FCSTD DOCUMENT  (FreeCAD 1.0R39319 (Git))
Label: master
License: All rights reserved
LicenseURL: https://en.wikipedia.org/wiki/All_rights_reserved
objects: Spreadsheet::Sheet×1, App::VarSet×1

FEATURE [Spreadsheet::Sheet] Spreadsheet  label="dims"
  cells = A1='inner chamber width; B1(iwChamber)=70; D1='brick thickness; E1=76; A2='outer chamber width; B2(owChamber)==B1 + 2 * E1; D2='brick width; E2=114; A3='chamber height; B3(hChamber)=150; D3='brick height; E3(hBrick)=210; A4='chamber base thickness; B4(tcBase)==E1; A5='chamber outer height; B5(hcWall)==B3 + B4; D5='extrusion width; E5(wExt)=20; D6='upper height; E6=40; A7='upper panel thickness; B7(tUpperPanel)=2; D7='lower height; E7=20; A8='lower panel thickness; B8(tLowerPanel)=2; A9='base thickness; B9(tBase)=3; D9='chamber proud; E9(brickProud)=5; D10='chamber top thickness; E10(tTop)=3; D11='upper panel trim; E11(uPanelTrim)==E9 + E10 + B7; A12='rockwool thickness; B12(tRockwool)=100; D12='upper panel height; E12(hUpPanel)==B9 + 20 + B5 - E11; A14='frame base width; B14(iwFurnace)==B2 + 2 * B12; A15='chamber edge length; B15(opChamber)==B2 / (1 + sqrt(2)); A16='furnace edge length; B16(opFurnace)==B14 / (1 + sqrt(2)); A18='lower chamber height; B18(lcHeight)=200; A19='lower brace height; B19(lvBrace)==B18 + E6 + E7
FEATURE [App::VarSet] VarSet  label="frameDims"
  Base_panelWidth = 174.798
  baseWidth = 422
  expr: Base_panelWidth = baseWidth / (1 + sqrt(2))
